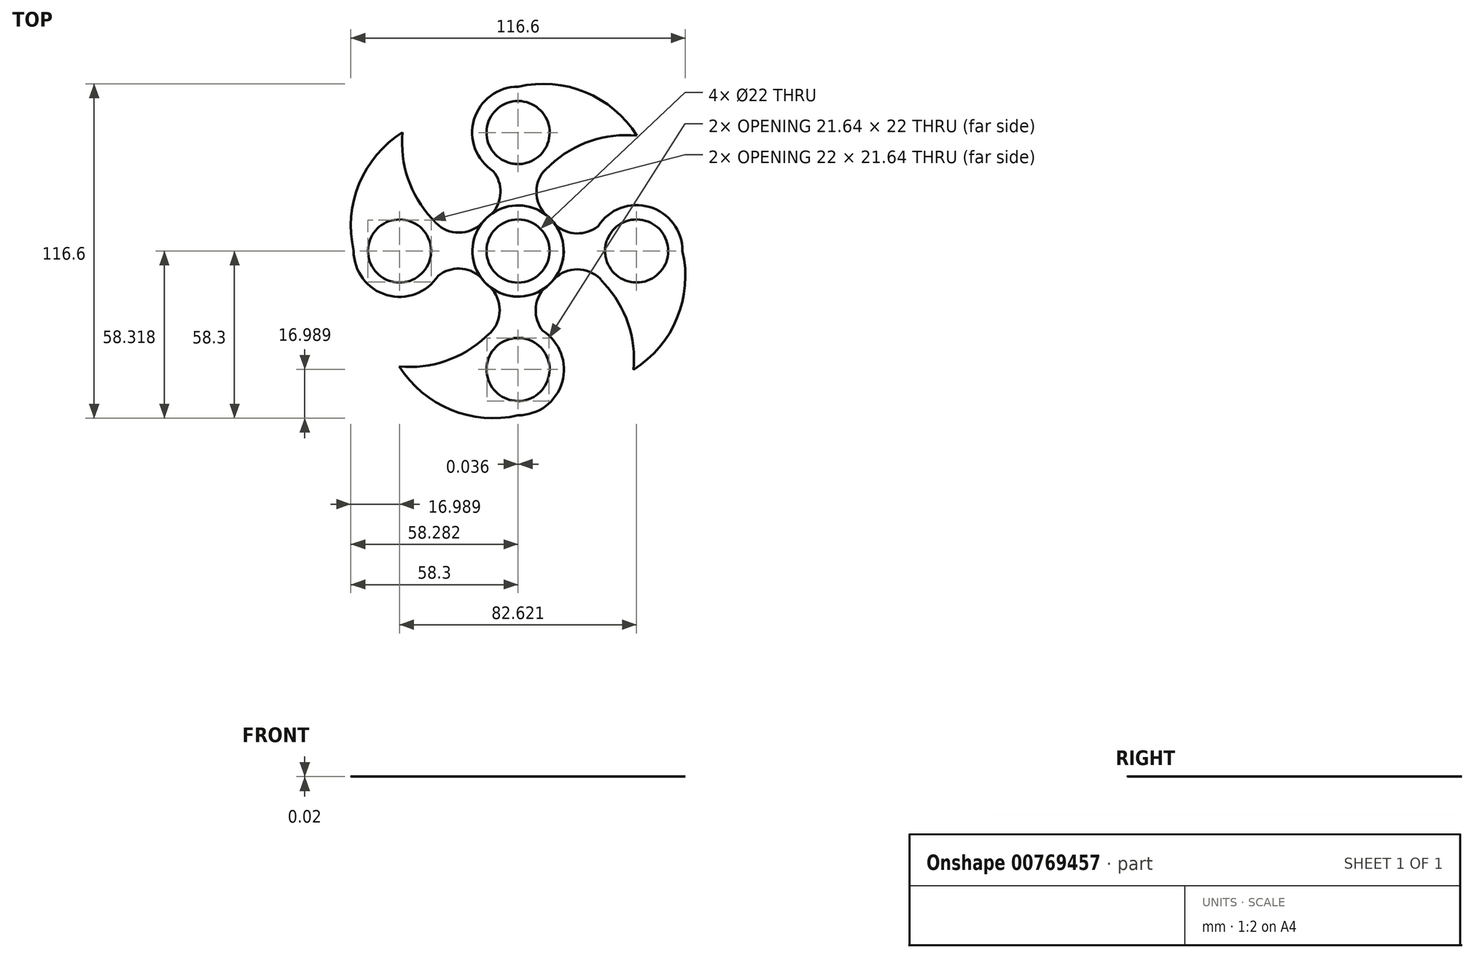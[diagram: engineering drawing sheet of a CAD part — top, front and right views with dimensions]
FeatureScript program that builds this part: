
annotation { "Feature Type Name" : "Feature", "Feature Type Description" : "" }
export const myFeature = defineFeature(function(context is Context, id is Id, definition is map)
    precondition{}
    {
        {
            var Q0;
            Q0=qCreatedBy(makeId("Top.planeOp"),FACE);
            var sketch = newSketch(context, id + "F0", { "sketchPlane" : qUnion([Q0])});
            skCircle(sketch, "E0", {"center": v(0, 0) * mm, "radius": 11 * mm});
            skCircle(sketch, "E1", {"center": v(0, 0) * mm, "radius": 15.91 * mm});
            skCircle(sketch, "E2", {"center": v(0, 41.31) * mm, "radius": 11 * mm});
            skCircle(sketch, "E3", {"center": v(0, 41.31) * mm, "radius": 15.99 * mm});
            skArc(sketch, "E4", {"start": v(-3.95, 31.05) * mm, "mid": v(-0.1, 30.31) * mm, "end": v(3.76, 30.98) * mm});
            skArc(sketch, "E5", {"start": v(41.4, 40.23) * mm, "mid": v(23.43, 55.4) * mm, "end": v(0, 57.3) * mm});
            skArc(sketch, "E6", {"start": v(41.4, 40.23) * mm, "mid": v(25.08, 38.31) * mm, "end": v(11.05, 29.75) * mm});
            skArc(sketch, "E7", {"start": v(11.05, 29.75) * mm, "mid": v(15, 47.33) * mm, "end": v(0, 57.3) * mm});
            skArc(sketch, "E8", {"start": v(11.05, 29.75) * mm, "mid": v(6.4, 20.6) * mm, "end": v(11.05, 11.45) * mm});
            skArc(sketch, "E9", {"start": v(-9.06, 13.08) * mm, "mid": v(-6.14, 20.39) * mm, "end": v(-8.63, 27.85) * mm});
            skSolve(sketch);
        }
        {
            var Q0;
            Q0 = qSketchRegion(id + "F0", true);
            extrude(context, id + "F1", {"entities" : qUnion([Q0]), "depth" : 1 / 50.8 * mm, "offsetDistance" : 25.4 * mm});
        }
        {
            var Q0;
            Q0=qCreatedBy(makeId("Front.planeOp"),FACE);
            var sketch = newSketch(context, id + "F2", { "sketchPlane" : qUnion([Q0])});
            skLineSegment(sketch, "E10", {"start": v(0, 0) * mm, "end": v(0, -24.42) * mm, "construction": true});
            skSolve(sketch);
        }
        {
            var Q0;
            Q0=makeQuery(id+"F1.opExtrude","SWEPT_BODY",BODY,{"disambiguationData":[OSD([sQuery(id+"F0.wireOp",EDGE,"E0"),sQuery(id+"F0.wireOp",EDGE,"E1"),sQuery(id+"F0.wireOp",EDGE,"E2"),sQuery(id+"F0.wireOp",EDGE,"E3"),sQuery(id+"F0.wireOp",EDGE,"E4"),sQuery(id+"F0.wireOp",EDGE,"E5"),sQuery(id+"F0.wireOp",EDGE,"E6"),sQuery(id+"F0.wireOp",EDGE,"E7"),sQuery(id+"F0.wireOp",EDGE,"E8"),sQuery(id+"F0.wireOp",EDGE,"E9")])]});
            var Q1;
            Q1=sQuery(id+"F2.wireOp",EDGE,"E10");
            circularPattern(context, id + "F3", {"entities" : qUnion([Q0]), "axis" : qUnion([Q1]), "angle" : 360 * degree, "instanceCount" : 4, "equalSpace" : true});
        }
    });
